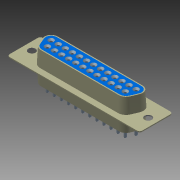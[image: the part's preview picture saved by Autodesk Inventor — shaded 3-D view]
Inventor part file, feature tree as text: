
AUTODESK INVENTOR PART (.ipt)
format: ipt  version: 2015 (Build 190159000, 159)  size: 296,448 bytes
history: native  units: in
note: dims shown in document units (in); Inventor stores cm internally (conversion verified against a paired STEP export)
features: sketch x5, extrude x3, mirror x1, other x1, imported_body x1
ambient origin geometry x8: Origin, YZ Plane, XZ Plane, XY Plane, X Axis, Y Axis, Z Axis, Center Point
bodies: Body1 (feature_tree)
feature tree (11):
  mirror  "Mirror1"
  other  "DB25_F1"
  extrude  "Extrusion1"  Depth=0.2323in TaperAngle=0.0deg
  extrude  "Extrusion2"  Depth=0.1181in
  sketch  "Sketch3"  dims[d6=0.2323in d7=0.0in]
  extrude  "Extrusion3"  [1 undecoded]
  sketch  "Sketch5"
  imported_body  "Base1"
  sketch  "Sketch1"  dims[d0=0.2323in d1=0.0in d2=0.2323in d3=0.0in]
  sketch  "Sketch2"  dims[d4=0.1181in d5=0.1181in]
  sketch  "Sketch4"
note: 1 required parameter value undecoded (feature->parameter linkage not recoverable at this tier; creation-order binding heuristic only, values carry confidence <= 0.55)
